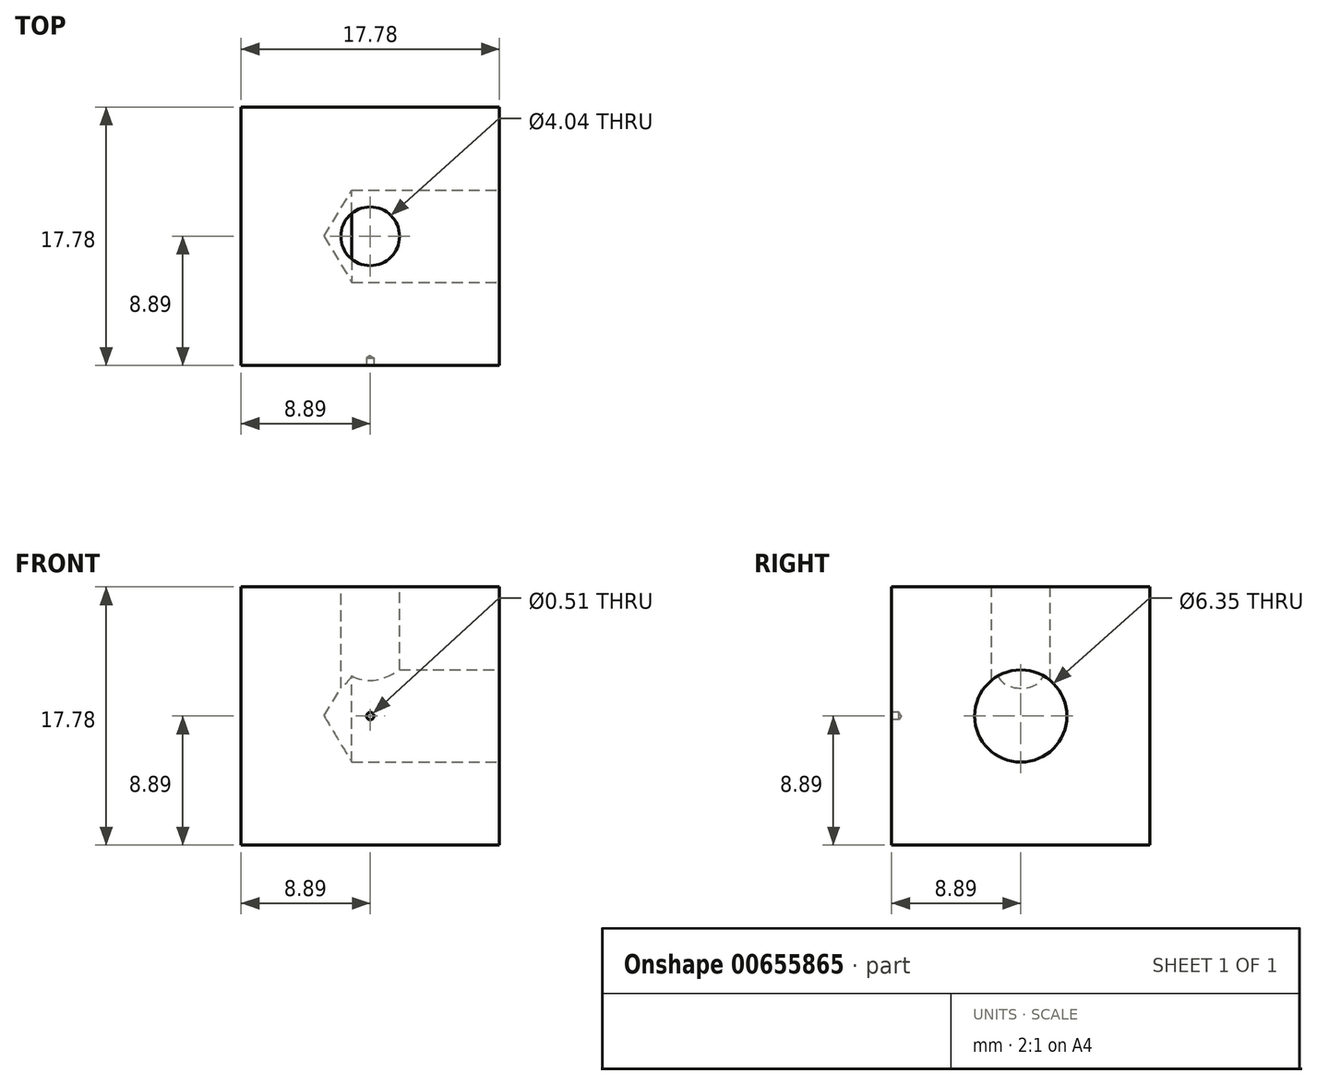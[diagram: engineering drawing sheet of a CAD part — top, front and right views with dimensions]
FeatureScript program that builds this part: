
annotation { "Feature Type Name" : "Feature", "Feature Type Description" : "" }
export const myFeature = defineFeature(function(context is Context, id is Id, definition is map)
    precondition{}
    {
        {
            var Q0;
            Q0=qCreatedBy(makeId("Front.planeOp"),FACE);
            var sketch = newSketch(context, id + "F0", { "sketchPlane" : qUnion([Q0])});
            skLineSegment(sketch, "E0.bottom", {"start": v(-8.9, -8.9) * mm, "end": v(8.9, -8.9) * mm});
            skLineSegment(sketch, "E0.top", {"start": v(-8.9, 8.9) * mm, "end": v(8.89, 8.9) * mm});
            skLineSegment(sketch, "E0.left", {"start": v(-8.9, -8.9) * mm, "end": v(-8.9, 8.9) * mm});
            skLineSegment(sketch, "E0.right", {"start": v(8.89, -8.9) * mm, "end": v(8.89, 8.9) * mm});
            skPoint(sketch, "E0.middle", {"position": v(0, 0) * mm});
            skSolve(sketch);
        }
        {
            var Q0;
            Q0 = qSketchRegion(id + "F0", true);
            extrude(context, id + "F1", {"entities" : qUnion([Q0]), "endBound" : BoundingType.SYMMETRIC, "depth" : 17.78 * mm, "offsetDistance" : 25.4 * mm});
        }
        {
            var Q0;
            Q0=makeQuery(id+"F1.opExtrude","CAP_FACE",FACE,{"disambiguationData":[OSD([sQuery(id+"F0.wireOp",EDGE,"E0.bottom"),sQuery(id+"F0.wireOp",EDGE,"E0.top"),sQuery(id+"F0.wireOp",EDGE,"E0.left"),sQuery(id+"F0.wireOp",EDGE,"E0.right")])],"isStart":false});
            var sketch = newSketch(context, id + "F2", { "sketchPlane" : qUnion([Q0])});
            skPoint(sketch, "E1", {"position": v(0, 0) * mm});
            skSolve(sketch);
        }
        {
            var Q0;
            Q0=makeQuery(id+"F1.opExtrude","SWEPT_FACE",FACE,{"disambiguationData":[OSD([sQuery(id+"F0.wireOp",EDGE,"E0.right")])]});
            var sketch = newSketch(context, id + "F3", { "sketchPlane" : qUnion([Q0])});
            skPoint(sketch, "E2", {"position": v(0, 0) * mm});
            skSolve(sketch);
        }
        {
            var Q0;
            Q0=makeQuery(id+"F1.opExtrude","SWEPT_FACE",FACE,{"disambiguationData":[OSD([sQuery(id+"F0.wireOp",EDGE,"E0.top")])]});
            var sketch = newSketch(context, id + "F4", { "sketchPlane" : qUnion([Q0])});
            skPoint(sketch, "E3", {"position": v(0, 0) * mm});
            skSolve(sketch);
        }
        {
            var Q0;
            Q0=sQuery(id+"F2.wireOp",VERTEX,"E1");
            var Q1;
            Q1=makeQuery(id+"F1.opExtrude","SWEPT_BODY",BODY,{"disambiguationData":[OSD([sQuery(id+"F0.wireOp",EDGE,"E0.bottom"),sQuery(id+"F0.wireOp",EDGE,"E0.top"),sQuery(id+"F0.wireOp",EDGE,"E0.left"),sQuery(id+"F0.wireOp",EDGE,"E0.right")])]});
            hole(context, id + "F5", {"style" : HoleStyle.SIMPLE, "endStyle" : HoleEndStyle.BLIND, "holeDiameter" : 0.5 * mm, "majorDiameter" : 6.35 * mm, "holeDepth" : 0.5 * mm, "tappedDepth" : 12.7 * mm, "tapClearance" : 3, "locations" : qUnion([Q0]), "scope" : qUnion([Q1])});
        }
        {
            var Q0;
            Q0=sQuery(id+"F4.wireOp",VERTEX,"E3");
            var Q1;
            Q1=makeQuery(id+"F1.opExtrude","SWEPT_BODY",BODY,{"disambiguationData":[OSD([sQuery(id+"F0.wireOp",EDGE,"E0.bottom"),sQuery(id+"F0.wireOp",EDGE,"E0.top"),sQuery(id+"F0.wireOp",EDGE,"E0.left"),sQuery(id+"F0.wireOp",EDGE,"E0.right")])]});
            hole(context, id + "F6", {"style" : HoleStyle.SIMPLE, "endStyle" : HoleEndStyle.BLIND, "holeDiameter" : 4.04 * mm, "majorDiameter" : 6.35 * mm, "holeDepth" : 10.16 * mm, "tappedDepth" : 12.7 * mm, "tapClearance" : 3, "locations" : qUnion([Q0]), "scope" : qUnion([Q1])});
        }
        {
            var Q0;
            Q0=sQuery(id+"F3.wireOp",VERTEX,"E2");
            var Q1;
            Q1=makeQuery(id+"F1.opExtrude","SWEPT_BODY",BODY,{"disambiguationData":[OSD([sQuery(id+"F0.wireOp",EDGE,"E0.bottom"),sQuery(id+"F0.wireOp",EDGE,"E0.top"),sQuery(id+"F0.wireOp",EDGE,"E0.left"),sQuery(id+"F0.wireOp",EDGE,"E0.right")])]});
            hole(context, id + "F7", {"style" : HoleStyle.SIMPLE, "endStyle" : HoleEndStyle.BLIND, "holeDiameter" : 6.35 * mm, "majorDiameter" : 6.35 * mm, "holeDepth" : 10.16 * mm, "tappedDepth" : 12.7 * mm, "tapClearance" : 3, "locations" : qUnion([Q0]), "scope" : qUnion([Q1])});
        }
    });
